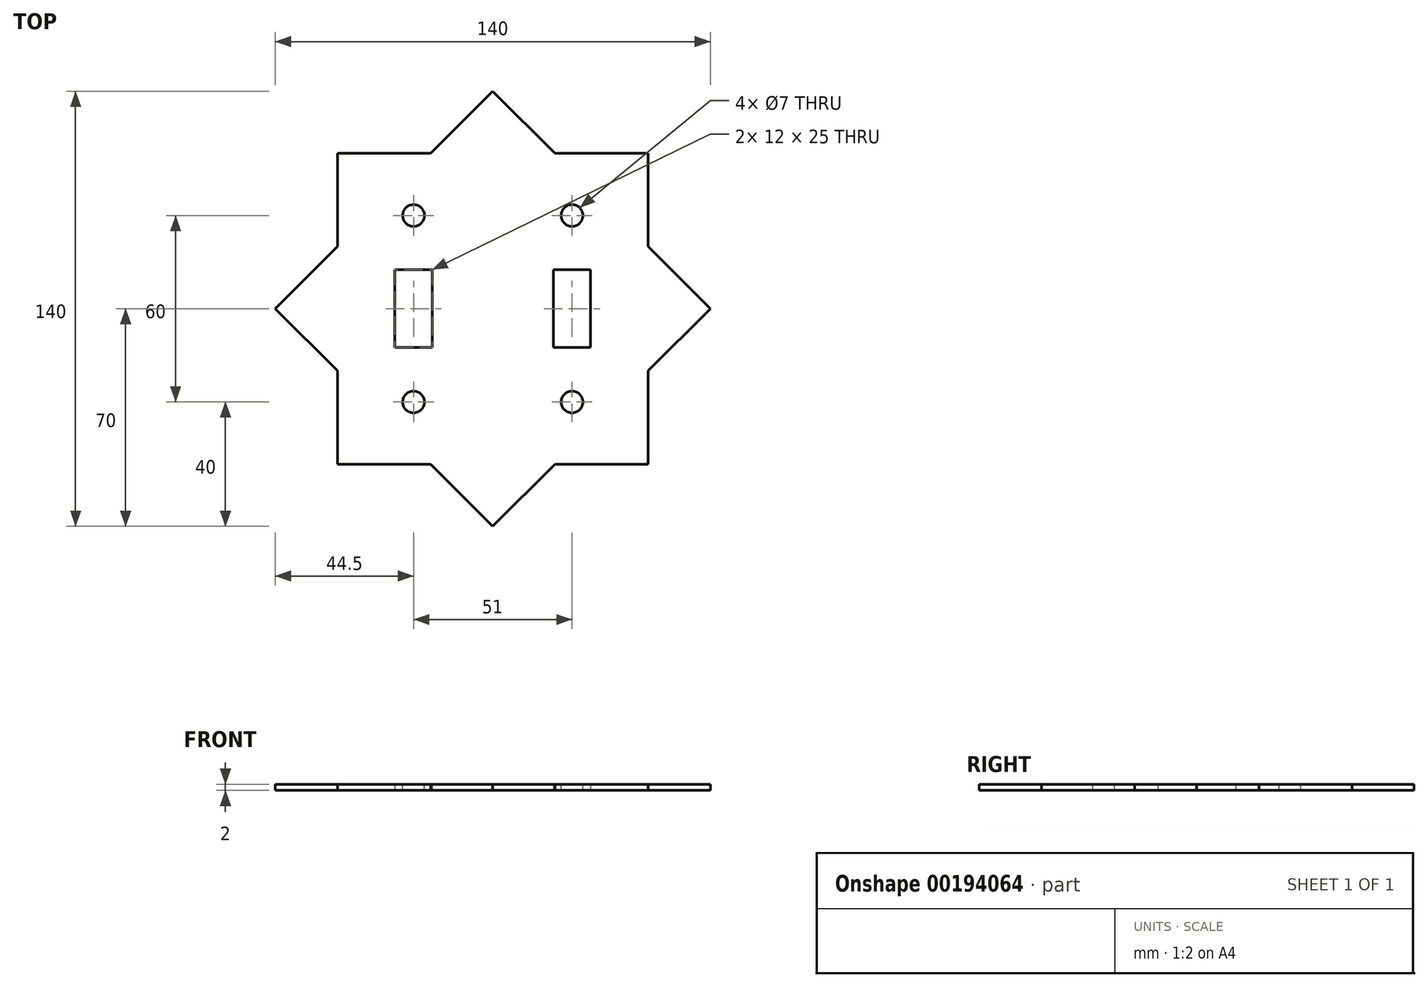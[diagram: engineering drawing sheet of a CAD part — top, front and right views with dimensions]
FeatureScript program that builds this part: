
annotation { "Feature Type Name" : "Feature", "Feature Type Description" : "" }
export const myFeature = defineFeature(function(context is Context, id is Id, definition is map)
    precondition{}
    {
        {
            var Q0;
            Q0=qCreatedBy(makeId("Top.planeOp"),FACE);
            var sketch = newSketch(context, id + "F0", { "sketchPlane" : qUnion([Q0])});
            skLineSegment(sketch, "E0.bottom", {"start": v(50, 50) * mm, "end": v(20, 50) * mm});
            skLineSegment(sketch, "E0.top", {"start": v(50, -50) * mm, "end": v(20, -50) * mm});
            skLineSegment(sketch, "E0.left", {"start": v(50, 50) * mm, "end": v(50, 20) * mm});
            skLineSegment(sketch, "E0.right", {"start": v(-50, 50) * mm, "end": v(-50, 20) * mm});
            skPoint(sketch, "E0.middle", {"position": v(0, 0) * mm});
            skCircle(sketch, "E1", {"center": v(-25.5, -30) * mm, "radius": 2.25 * mm});
            skCircle(sketch, "E2", {"center": v(-25.5, 30) * mm, "radius": 2.25 * mm});
            skLineSegment(sketch, "E3.bottom", {"start": v(-31.5, 12.5) * mm, "end": v(-19.5, 12.5) * mm});
            skLineSegment(sketch, "E3.top", {"start": v(-31.5, -12.5) * mm, "end": v(-19.5, -12.5) * mm});
            skLineSegment(sketch, "E3.left", {"start": v(-31.5, 12.5) * mm, "end": v(-31.5, -12.5) * mm});
            skLineSegment(sketch, "E3.right", {"start": v(-19.5, 12.5) * mm, "end": v(-19.5, -12.5) * mm});
            skLineSegment(sketch, "E4", {"start": v(-25.5, 30) * mm, "end": v(-25.5, -30) * mm, "construction": true});
            skLineSegment(sketch, "E5.MirrorCS", {"start": v(-19.5, -12.5) * mm, "end": v(-31.5, -12.5) * mm});
            skLineSegment(sketch, "E6.MirrorCS", {"start": v(-19.5, 12.5) * mm, "end": v(-31.5, 12.5) * mm});
            skCircle(sketch, "E7.MirrorC", {"center": v(25.5, 30) * mm, "radius": 2.25 * mm});
            skLineSegment(sketch, "E8.MirrorCS", {"start": v(31.5, 12.5) * mm, "end": v(31.5, -12.5) * mm});
            skLineSegment(sketch, "E9.MirrorCS", {"start": v(19.5, -12.5) * mm, "end": v(31.5, -12.5) * mm});
            skCircle(sketch, "E10.MirrorC", {"center": v(25.5, -30) * mm, "radius": 2.25 * mm});
            skLineSegment(sketch, "E11.MirrorCS", {"start": v(19.5, 12.5) * mm, "end": v(31.5, 12.5) * mm});
            skLineSegment(sketch, "E12.MirrorCS", {"start": v(19.5, 12.5) * mm, "end": v(19.5, -12.5) * mm});
            skLineSegment(sketch, "E13.MirrorCS", {"start": v(31.5, -12.5) * mm, "end": v(19.5, -12.5) * mm});
            skLineSegment(sketch, "E14.MirrorCS", {"start": v(31.5, 12.5) * mm, "end": v(19.5, 12.5) * mm});
            skLineSegment(sketch, "E15.MirrorCS", {"start": v(25.5, 30) * mm, "end": v(25.5, -30) * mm, "construction": true});
            skLineSegment(sketch, "E16", {"start": v(50, 20) * mm, "end": v(70, 0) * mm});
            skLineSegment(sketch, "E17", {"start": v(-20, 50) * mm, "end": v(0, 70) * mm});
            skLineSegment(sketch, "E18", {"start": v(0, 70) * mm, "end": v(20, 50) * mm});
            skLineSegment(sketch, "E19.MirrorCS", {"start": v(-20, -50) * mm, "end": v(0, -70) * mm});
            skLineSegment(sketch, "E20.MirrorCS", {"start": v(0, -70) * mm, "end": v(20, -50) * mm});
            skLineSegment(sketch, "E21.MirrorCS", {"start": v(50, -20) * mm, "end": v(70, 0) * mm});
            skLineSegment(sketch, "E22.MirrorCS", {"start": v(-50, 20) * mm, "end": v(-70, 0) * mm});
            skLineSegment(sketch, "E23.MirrorCS", {"start": v(-50, -20) * mm, "end": v(-70, 0) * mm});
            skLineSegment(sketch, "E24.trimOffspring", {"start": v(-50, -20) * mm, "end": v(-50, -50) * mm});
            skLineSegment(sketch, "E25.trimOffspring", {"start": v(50, -20) * mm, "end": v(50, -50) * mm});
            skLineSegment(sketch, "E26.trimOffspring", {"start": v(-20, -50) * mm, "end": v(-50, -50) * mm});
            skLineSegment(sketch, "E27.trimOffspring", {"start": v(-20, 50) * mm, "end": v(-50, 50) * mm});
            skPoint(sketch, "E28.MirrorCS.end.orphan", {"position": v(50, 34.57) * mm});
            skPoint(sketch, "E28.MirrorCS.start.orphan", {"position": v(70, 0) * mm});
            skPoint(sketch, "E29.orphan", {"position": v(50, -34.57) * mm});
            skSolve(sketch);
        }
        {
            var Q0;
            Q0=qSketchRegion(id+"F0",true);
            extrude(context, id + "F1", {"entities" : qUnion([Q0]), "depth" : 2 * mm});
        }
        {
            var Q0;
            Q0=makeQuery(id+"F1.opExtrude","CAP_FACE",FACE,{"disambiguationData":[OSD([sQuery(id+"F0.wireOp",EDGE,"E0.bottom"),sQuery(id+"F0.wireOp",EDGE,"E0.top"),sQuery(id+"F0.wireOp",EDGE,"E0.left"),sQuery(id+"F0.wireOp",EDGE,"E0.right"),sQuery(id+"F0.wireOp",EDGE,"E1"),sQuery(id+"F0.wireOp",EDGE,"E2"),sQuery(id+"F0.wireOp",EDGE,"E3.right"),sQuery(id+"F0.wireOp",EDGE,"E5.MirrorCS"),sQuery(id+"F0.wireOp",EDGE,"E3.left"),sQuery(id+"F0.wireOp",EDGE,"E6.MirrorCS"),sQuery(id+"F0.wireOp",EDGE,"E10.MirrorC"),sQuery(id+"F0.wireOp",EDGE,"E14.MirrorCS"),sQuery(id+"F0.wireOp",EDGE,"E7.MirrorC"),sQuery(id+"F0.wireOp",EDGE,"E8.MirrorCS"),sQuery(id+"F0.wireOp",EDGE,"E9.MirrorCS"),sQuery(id+"F0.wireOp",EDGE,"E12.MirrorCS"),sQuery(id+"F0.wireOp",EDGE,"E16"),sQuery(id+"F0.wireOp",EDGE,"E17"),sQuery(id+"F0.wireOp",EDGE,"E18"),sQuery(id+"F0.wireOp",EDGE,"E19.MirrorCS"),sQuery(id+"F0.wireOp",EDGE,"E20.MirrorCS"),sQuery(id+"F0.wireOp",EDGE,"E21.MirrorCS"),sQuery(id+"F0.wireOp",EDGE,"E22.MirrorCS"),sQuery(id+"F0.wireOp",EDGE,"E23.MirrorCS"),sQuery(id+"F0.wireOp",EDGE,"E24.trimOffspring"),sQuery(id+"F0.wireOp",EDGE,"E25.trimOffspring"),sQuery(id+"F0.wireOp",EDGE,"E26.trimOffspring"),sQuery(id+"F0.wireOp",EDGE,"E27.trimOffspring")])],"isStart":false});
            var sketch = newSketch(context, id + "F2", { "sketchPlane" : qUnion([Q0])});
            skCircle(sketch, "E30", {"center": v(-25.5, 30) * mm, "radius": 3.5 * mm});
            skCircle(sketch, "E31", {"center": v(25.5, 30) * mm, "radius": 3.5 * mm});
            skCircle(sketch, "E32", {"center": v(25.5, -30) * mm, "radius": 3.5 * mm});
            skCircle(sketch, "E33", {"center": v(-25.5, -30) * mm, "radius": 3.5 * mm});
            skSolve(sketch);
        }
        {
            var Q0;
            Q0=qSketchRegion(id+"F2",true);
            extrude(context, id + "F3", {"entities" : qUnion([Q0]), "operationType" : NewBodyOperationType.REMOVE, "oppositeDirection" : true, "depth" : 2 * mm});
        }
    });
